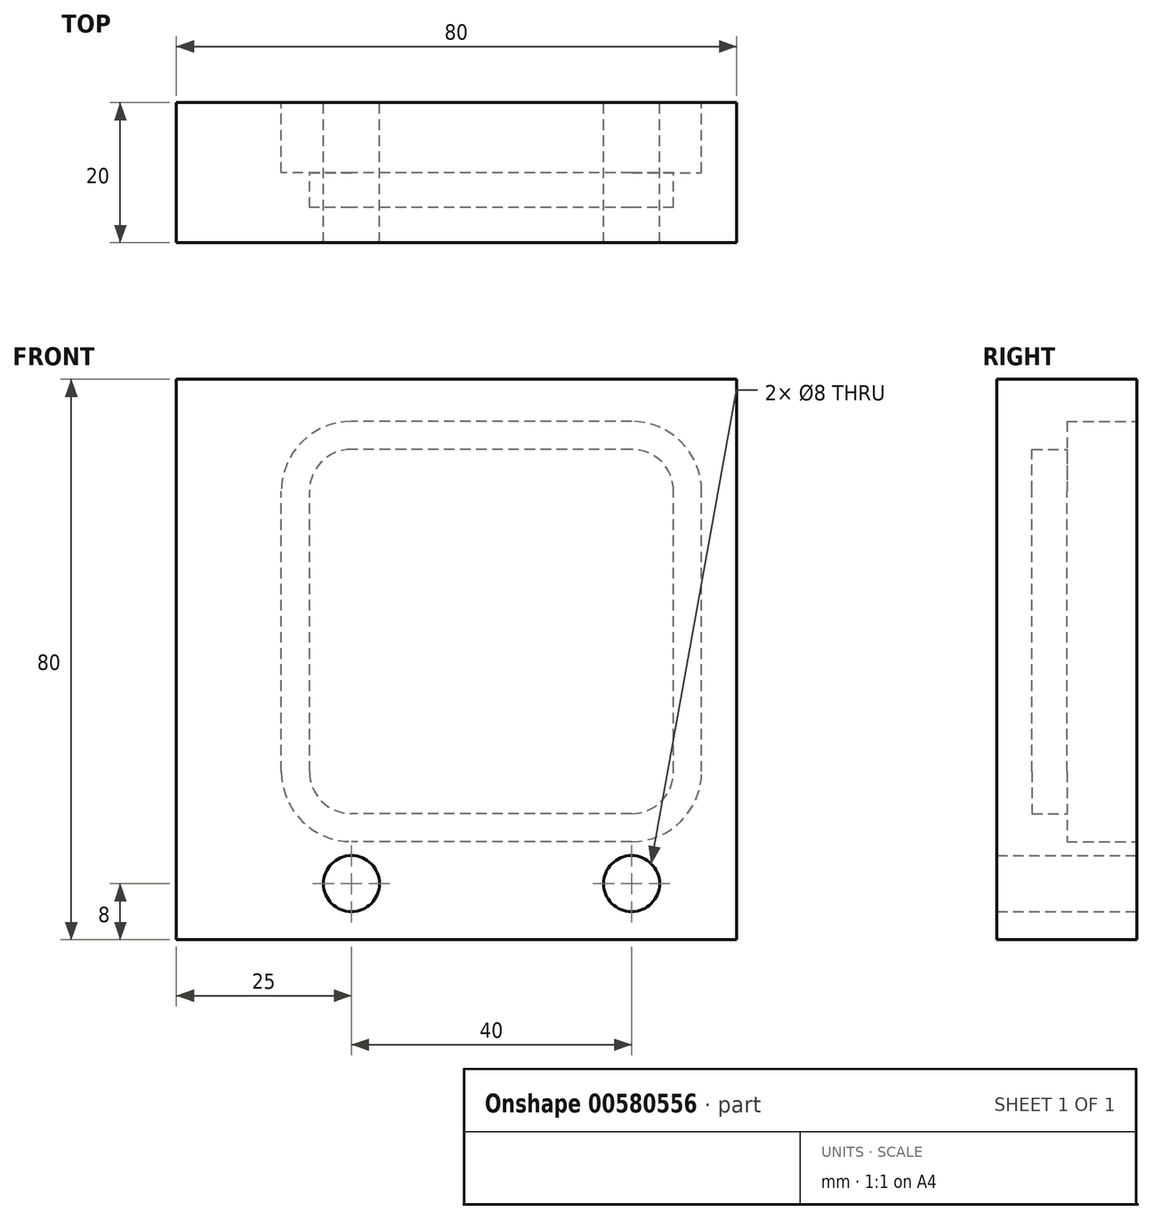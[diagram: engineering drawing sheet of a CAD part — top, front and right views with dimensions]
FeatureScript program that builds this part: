
annotation { "Feature Type Name" : "Feature", "Feature Type Description" : "" }
export const myFeature = defineFeature(function(context is Context, id is Id, definition is map)
    precondition{}
    {
        {
            var Q0;
            Q0=qCreatedBy(makeId("Front.planeOp"),FACE);
            var sketch = newSketch(context, id + "F0", { "sketchPlane" : qUnion([Q0])});
            skLineSegment(sketch, "E0.bottom", {"start": v(35, 0) * mm, "end": v(-45, 0) * mm});
            skLineSegment(sketch, "E0.top", {"start": v(35, -80) * mm, "end": v(-45, -80) * mm});
            skLineSegment(sketch, "E0.left", {"start": v(35, 0) * mm, "end": v(35, -80) * mm});
            skLineSegment(sketch, "E0.right", {"start": v(-45, 0) * mm, "end": v(-45, -80) * mm});
            skSolve(sketch);
        }
        {
            var Q0;
            Q0=makeQuery(id+"F0.imprint","IMPRINT",FACE,{"disambiguationData":[TD([[makeQuery(id+"F0.imprint","IMPRINT",EDGE,{"derivedFrom":sQuery(id+"F0.wireOp",EDGE,"E0.bottom")}),1.0]])]});
            extrude(context, id + "F1", {"entities" : qUnion([Q0]), "depth" : 20 * mm, "offsetDistance" : 25 * mm});
        }
        {
            var Q0;
            Q0=makeQuery(id+"F1.opExtrude","CAP_FACE",FACE,{"disambiguationData":[OSD([sQuery(id+"F0.wireOp",EDGE,"E0.bottom"),sQuery(id+"F0.wireOp",EDGE,"E0.top"),sQuery(id+"F0.wireOp",EDGE,"E0.left"),sQuery(id+"F0.wireOp",EDGE,"E0.right")])],"isStart":true});
            var sketch = newSketch(context, id + "F2", { "sketchPlane" : qUnion([Q0])});
            skLineSegment(sketch, "E1.bottom", {"start": v(-20, -62) * mm, "end": v(20, -62) * mm});
            skLineSegment(sketch, "E1.top", {"start": v(-20, -10) * mm, "end": v(20, -10) * mm});
            skLineSegment(sketch, "E1.left", {"start": v(-26, -56) * mm, "end": v(-26, -16) * mm});
            skLineSegment(sketch, "E1.right", {"start": v(26, -56) * mm, "end": v(26, -16) * mm});
            skArc(sketch, "E2", {"start": v(-20, -10) * mm, "mid": v(-24.24, -11.76) * mm, "end": v(-26, -16) * mm});
            skArc(sketch, "E3", {"start": v(-26, -56) * mm, "mid": v(-24.24, -60.24) * mm, "end": v(-20, -62) * mm});
            skArc(sketch, "E4", {"start": v(20, -62) * mm, "mid": v(24.24, -60.24) * mm, "end": v(26, -56) * mm});
            skArc(sketch, "E5", {"start": v(26, -16) * mm, "mid": v(24.24, -11.76) * mm, "end": v(20, -10) * mm});
            skSolve(sketch);
        }
        {
            var Q0;
            Q0=makeQuery(id+"F2.imprint","IMPRINT",FACE,{"disambiguationData":[TD([[makeQuery(id+"F2.imprint","IMPRINT",EDGE,{"derivedFrom":sQuery(id+"F2.wireOp",EDGE,"E1.bottom")}),1.0]])]});
            extrude(context, id + "F3", {"entities" : qUnion([Q0]), "operationType" : NewBodyOperationType.REMOVE, "oppositeDirection" : true, "depth" : 15 * mm, "offsetDistance" : 25 * mm});
        }
        {
            var Q0;
            Q0=makeQuery(id+"F1.opExtrude","CAP_FACE",FACE,{"disambiguationData":[OSD([sQuery(id+"F0.wireOp",EDGE,"E0.bottom"),sQuery(id+"F0.wireOp",EDGE,"E0.top"),sQuery(id+"F0.wireOp",EDGE,"E0.left"),sQuery(id+"F0.wireOp",EDGE,"E0.right")])],"isStart":true});
            var sketch = newSketch(context, id + "F4", { "sketchPlane" : qUnion([Q0])});
            skLineSegment(sketch, "E6.bottom", {"start": v(-20, -66) * mm, "end": v(20, -66) * mm});
            skLineSegment(sketch, "E6.top", {"start": v(-20, -6) * mm, "end": v(20, -6) * mm});
            skLineSegment(sketch, "E6.left", {"start": v(-30, -56) * mm, "end": v(-30, -16) * mm});
            skLineSegment(sketch, "E6.right", {"start": v(30, -56) * mm, "end": v(30, -16) * mm});
            skArc(sketch, "E7", {"start": v(-30, -56) * mm, "mid": v(-27.07, -63.07) * mm, "end": v(-20, -66) * mm});
            skArc(sketch, "E8", {"start": v(-20, -6) * mm, "mid": v(-27.07, -8.93) * mm, "end": v(-30, -16) * mm});
            skArc(sketch, "E9", {"start": v(30, -16) * mm, "mid": v(27.07, -8.93) * mm, "end": v(20, -6) * mm});
            skArc(sketch, "E10", {"start": v(20, -66) * mm, "mid": v(27.07, -63.07) * mm, "end": v(30, -56) * mm});
            skSolve(sketch);
        }
        {
            var Q0;
            Q0=makeQuery(id+"F4.imprint","IMPRINT",FACE,{"disambiguationData":[TD([[makeQuery(id+"F4.imprint","IMPRINT",EDGE,{"derivedFrom":sQuery(id+"F4.wireOp",EDGE,"E6.bottom")}),1.0]])]});
            extrude(context, id + "F5", {"entities" : qUnion([Q0]), "operationType" : NewBodyOperationType.REMOVE, "oppositeDirection" : true, "depth" : 10 * mm, "offsetDistance" : 25 * mm});
        }
        {
            var Q0;
            Q0=makeQuery(id+"F1.opExtrude","CAP_FACE",FACE,{"disambiguationData":[OSD([sQuery(id+"F0.wireOp",EDGE,"E0.bottom"),sQuery(id+"F0.wireOp",EDGE,"E0.top"),sQuery(id+"F0.wireOp",EDGE,"E0.left"),sQuery(id+"F0.wireOp",EDGE,"E0.right")])],"isStart":true});
            var sketch = newSketch(context, id + "F6", { "sketchPlane" : qUnion([Q0])});
            skCircle(sketch, "E11", {"center": v(-20, -72) * mm, "radius": 4 * mm});
            skCircle(sketch, "E12", {"center": v(20, -72) * mm, "radius": 4 * mm});
            skSolve(sketch);
        }
        {
            var Q0;
            Q0 = qSketchRegion(id + "F6", true);
            extrude(context, id + "F7", {"entities" : qUnion([Q0]), "operationType" : NewBodyOperationType.REMOVE, "endBound" : BoundingType.THROUGH_ALL, "oppositeDirection" : true, "depth" : 25 * mm, "offsetDistance" : 25 * mm});
        }
    });
